# Revit family: Haworth_BuzziHub_Table_Occasional
name_source: partatom
category: Furniture
revit_build: Autodesk Revit 2018 (Build: 20170223_1515(x64)
units: mm (PartAtom-declared; Revit-internal decimal feet)

## family parameters
Always vertical = Yes
Cut with Voids When Loaded = No
OmniClass Number = 23.40.70.14.64.21
OmniClass Title = Systems Furniture
Room Calculation Point = No
Shared = No
Work Plane-Based = No

## types (3) — shared parameters
Assembly Code = E2020200
Manufacturer = Haworth
Model = HCBZ-HBTO
Revision Number = 1
Size = Verify Final Dim. w/ Haworth
URL = http://www.haworth.com
URL - Product = https://www.haworth.com
Warranty = http://www.haworth.com

## per-type parameters (varying)
| type | Actual Depth | Actual Height | Actual Width | Description | Large | Medium | Small |
| HCBZ-HBTO-2 | 16 9/64" | 26 197/256" | 33 169/256" | Haworth BuzziHub Table Medium Occasional Table | No | Yes | No |
| HCBZ-HBTO-1 | 15 3/4" | 26 197/256" | 18 1/2" | Haworth BuzziHub Table Small Occasional Table | No | No | Yes |
| HCBZ-HBTO-3 | 17 23/32" | 21 83/128" | 54 17/32" | Haworth BuzziHub Table - Large Occasional Table | Yes | No | No |

## geometry (parser evidence)
native form markers: Sweep x3
no freeform markers — native parametric forms only
